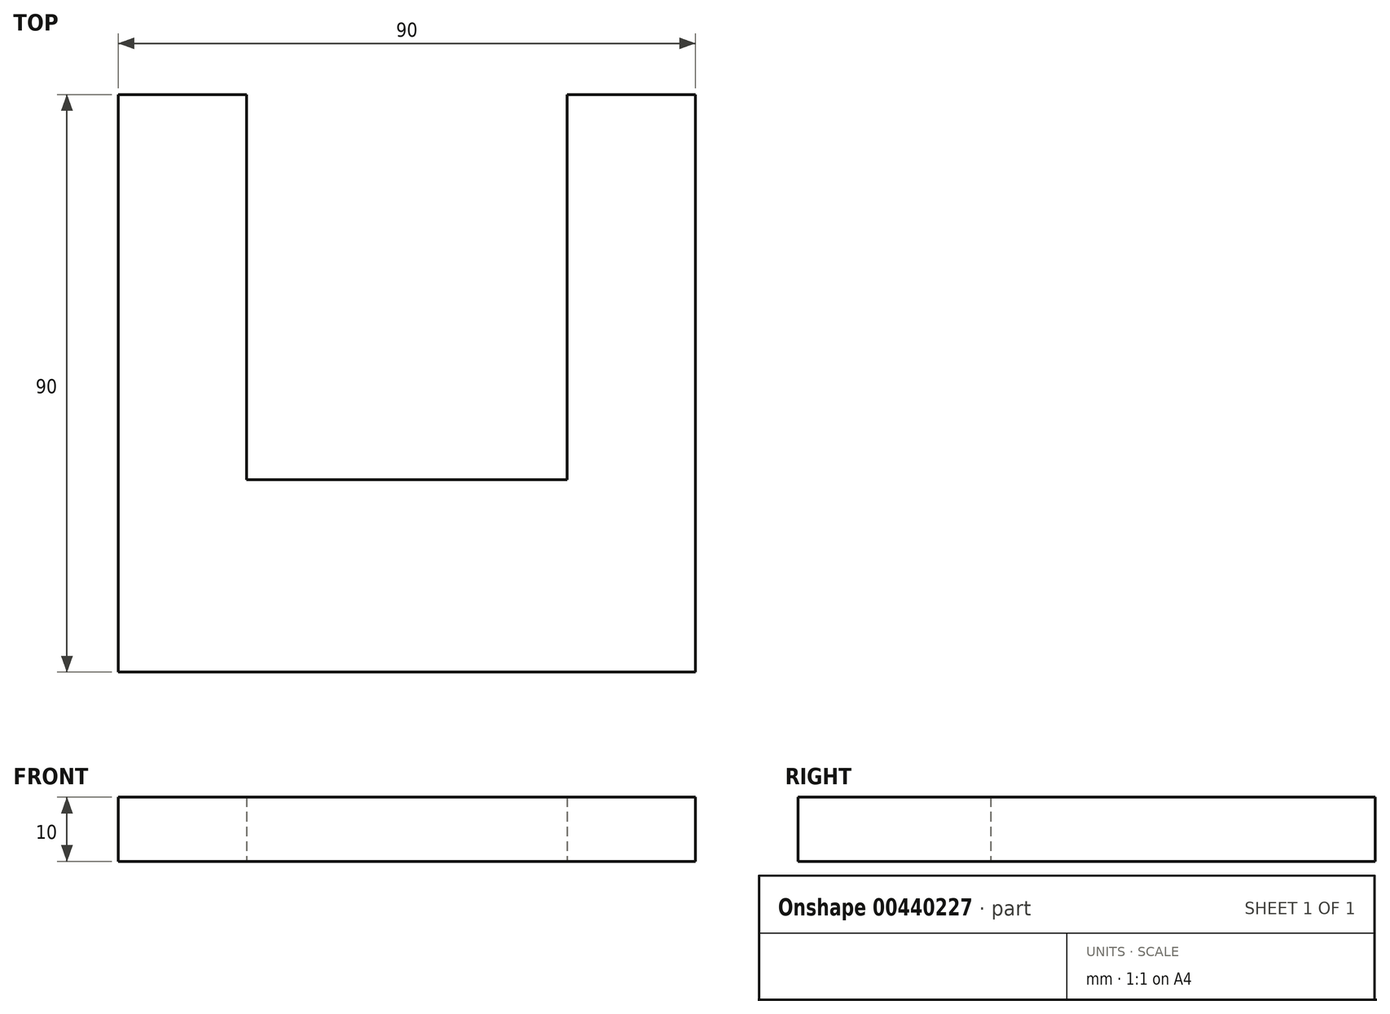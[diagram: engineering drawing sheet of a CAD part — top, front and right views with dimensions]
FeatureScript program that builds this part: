
annotation { "Feature Type Name" : "Feature", "Feature Type Description" : "" }
export const myFeature = defineFeature(function(context is Context, id is Id, definition is map)
    precondition{}
    {
        {
            var Q0;
            Q0=qCreatedBy(makeId("Top.planeOp"),FACE);
            var sketch = newSketch(context, id + "F0", { "sketchPlane" : qUnion([Q0])});
            skLineSegment(sketch, "E0.bottom", {"start": v(-25, 15) * mm, "end": v(25, 15) * mm});
            skLineSegment(sketch, "E0.top", {"start": v(-25, -15) * mm, "end": v(25, -15) * mm});
            skLineSegment(sketch, "E0.left", {"start": v(-25, 15) * mm, "end": v(-25, -15) * mm});
            skLineSegment(sketch, "E0.right", {"start": v(25, 15) * mm, "end": v(25, -15) * mm});
            skPoint(sketch, "E0.middle", {"position": v(0, 0) * mm});
            skLineSegment(sketch, "E1.bottom", {"start": v(25, -15) * mm, "end": v(45, -15) * mm});
            skLineSegment(sketch, "E1.top", {"start": v(25, 75) * mm, "end": v(45, 75) * mm});
            skLineSegment(sketch, "E1.left", {"start": v(25, -15) * mm, "end": v(25, 75) * mm});
            skLineSegment(sketch, "E1.right", {"start": v(45, -15) * mm, "end": v(45, 75) * mm});
            skLineSegment(sketch, "E2.bottom", {"start": v(-25, -15) * mm, "end": v(-45, -15) * mm});
            skLineSegment(sketch, "E2.top", {"start": v(-25, 75) * mm, "end": v(-45, 75) * mm});
            skLineSegment(sketch, "E2.left", {"start": v(-25, -15) * mm, "end": v(-25, 75) * mm});
            skLineSegment(sketch, "E2.right", {"start": v(-45, -15) * mm, "end": v(-45, 75) * mm});
            skSolve(sketch);
        }
        {
            var Q0;
            Q0 = qSketchRegion(id + "F0", true);
            extrude(context, id + "F1", {"entities" : qUnion([Q0]), "depth" : 10 * mm});
        }
    });
